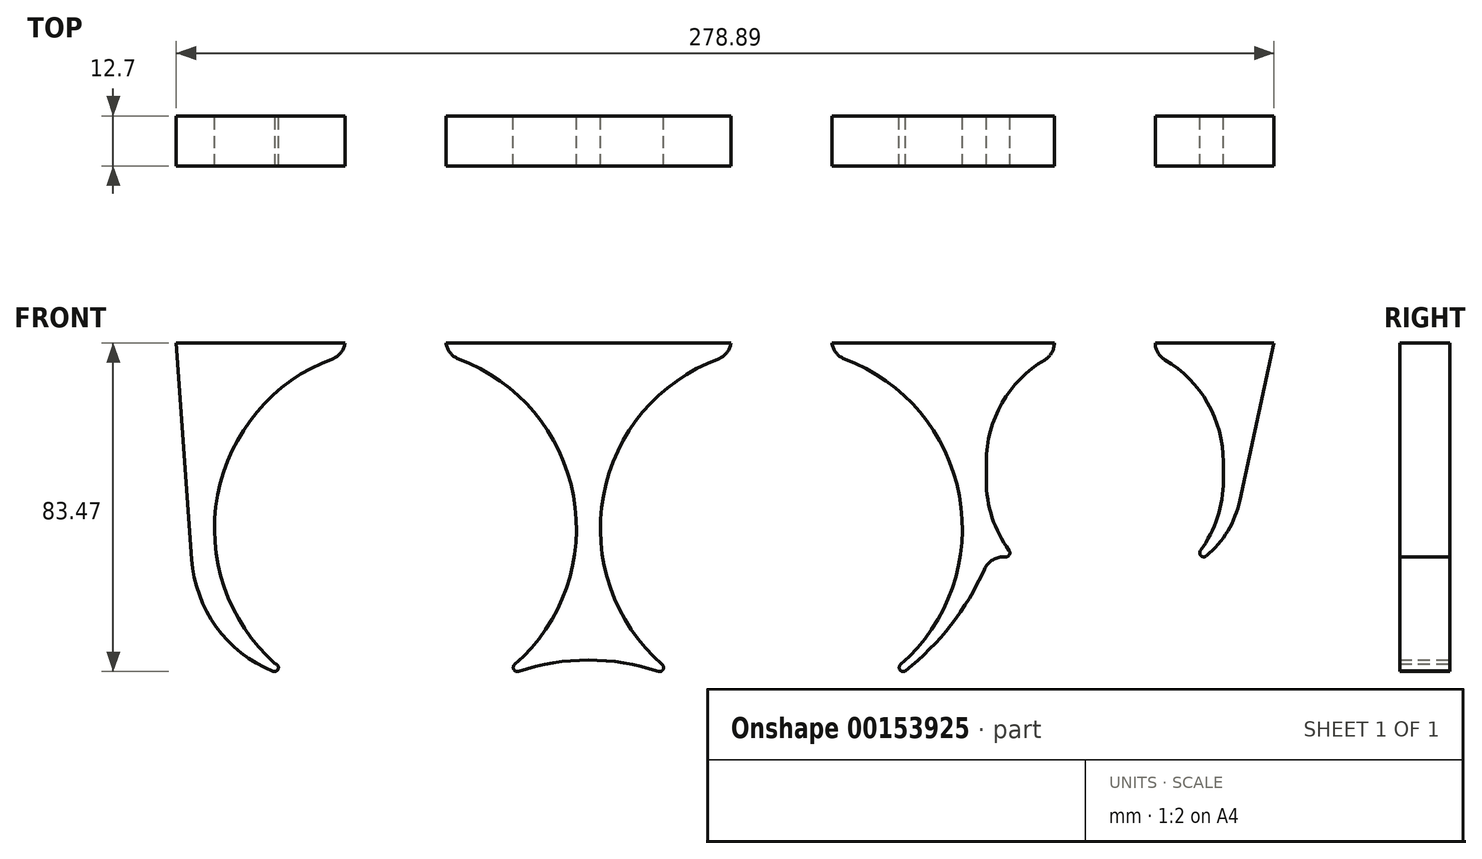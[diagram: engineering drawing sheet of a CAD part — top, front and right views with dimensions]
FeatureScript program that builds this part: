
annotation { "Feature Type Name" : "Feature", "Feature Type Description" : "" }
export const myFeature = defineFeature(function(context is Context, id is Id, definition is map)
    precondition{}
    {
        {
            var Q0;
            Q0=qCreatedBy(makeId("Front.planeOp"),FACE);
            var sketch = newSketch(context, id + "F0", { "sketchPlane" : qUnion([Q0])});
            skArc(sketch, "E0", {"start": v(-61.72, 44.05) * mm, "mid": v(-49.02, -45.85) * mm, "end": v(-36.32, 44.05) * mm, "construction": true});
            skArc(sketch, "E1", {"start": v(36.32, 44.05) * mm, "mid": v(49.02, -45.85) * mm, "end": v(61.72, 44.05) * mm, "construction": true});
            skLineSegment(sketch, "E2", {"start": v(-61.72, 44.05) * mm, "end": v(-61.72, 47.1) * mm, "construction": true});
            skLineSegment(sketch, "E3", {"start": v(-61.72, 47.1) * mm, "end": v(-36.32, 47.1) * mm, "construction": true});
            skLineSegment(sketch, "E4", {"start": v(-36.32, 47.1) * mm, "end": v(-36.32, 44.05) * mm, "construction": true});
            skLineSegment(sketch, "E5", {"start": v(36.32, 44.05) * mm, "end": v(36.32, 47.1) * mm, "construction": true});
            skLineSegment(sketch, "E6", {"start": v(36.32, 47.1) * mm, "end": v(61.72, 47.1) * mm, "construction": true});
            skLineSegment(sketch, "E7", {"start": v(61.72, 47.1) * mm, "end": v(61.72, 44.05) * mm, "construction": true});
            skArc(sketch, "E8", {"start": v(-65, 42.98) * mm, "mid": v(-62.78, 44.58) * mm, "end": v(-61.72, 47.1) * mm, "construction": true});
            skPoint(sketch, "E8.centerSnap0", {"position": v(-49.02, 47.1) * mm});
            skArc(sketch, "E9", {"start": v(-36.32, 47.1) * mm, "mid": v(-35.26, 44.58) * mm, "end": v(-33.05, 42.98) * mm, "construction": true});
            skArc(sketch, "E10", {"start": v(33.05, 42.98) * mm, "mid": v(35.26, 44.58) * mm, "end": v(36.32, 47.1) * mm, "construction": true});
            skArc(sketch, "E11", {"start": v(61.72, 47.1) * mm, "mid": v(62.78, 44.58) * mm, "end": v(65, 42.98) * mm, "construction": true});
            skArc(sketch, "E12", {"start": v(118.5, 44.05) * mm, "mid": v(105.9, 33) * mm, "end": v(101.22, 16.9) * mm, "construction": true});
            skLineSegment(sketch, "E13", {"start": v(118.5, 44.05) * mm, "end": v(118.5, 47.1) * mm, "construction": true});
            skLineSegment(sketch, "E14", {"start": v(118.5, 47.1) * mm, "end": v(143.9, 47.1) * mm, "construction": true});
            skLineSegment(sketch, "E15", {"start": v(143.9, 47.1) * mm, "end": v(143.9, 44.05) * mm, "construction": true});
            skArc(sketch, "E16", {"start": v(115.99, 42.73) * mm, "mid": v(117.82, 44.59) * mm, "end": v(118.5, 47.1) * mm, "construction": true});
            skArc(sketch, "E17", {"start": v(143.9, 47.1) * mm, "mid": v(144.56, 44.59) * mm, "end": v(146.4, 42.73) * mm, "construction": true});
            skArc(sketch, "E18", {"start": v(101.22, 12.13) * mm, "mid": v(131.2, -17.84) * mm, "end": v(161.16, 12.13) * mm, "construction": true});
            skArc(sketch, "E19.trimOffspring", {"start": v(161.16, 16.9) * mm, "mid": v(156.48, 33) * mm, "end": v(143.9, 44.05) * mm, "construction": true});
            skLineSegment(sketch, "E20", {"start": v(101.22, 16.9) * mm, "end": v(101.22, 12.13) * mm, "construction": true});
            skLineSegment(sketch, "E21", {"start": v(161.16, 12.13) * mm, "end": v(161.16, 16.9) * mm, "construction": true});
            skSolve(sketch);
        }
        {
            var Q0;
            Q0=qCreatedBy(makeId("Front.planeOp"),FACE);
            var sketch = newSketch(context, id + "F1", { "sketchPlane" : qUnion([Q0])});
            skLineSegment(sketch, "E22", {"start": v(-36.2, 47.1) * mm, "end": v(36.2, 47.1) * mm});
            skArc(sketch, "E23", {"start": v(-36.2, 47.1) * mm, "mid": v(-35.16, 44.65) * mm, "end": v(-33, 43.1) * mm});
            skArc(sketch, "E24", {"start": v(33, 43.1) * mm, "mid": v(35.16, 44.65) * mm, "end": v(36.2, 47.1) * mm});
            skArc(sketch, "E25", {"start": v(-18.74, -34.6) * mm, "mid": v(-3.8, 8.3) * mm, "end": v(-33, 43.1) * mm});
            skArc(sketch, "E26", {"start": v(33, 43.1) * mm, "mid": v(3.8, 8.3) * mm, "end": v(18.74, -34.6) * mm});
            skArc(sketch, "E27", {"start": v(17.75, -36.32) * mm, "mid": v(0, -33.44) * mm, "end": v(-17.75, -36.32) * mm});
            skPoint(sketch, "E28.visualSharp", {"position": v(-26.96, -40.34) * mm});
            skArc(sketch, "E28.filletArc", {"start": v(-18.74, -34.6) * mm, "mid": v(-18.95, -35.86) * mm, "end": v(-17.75, -36.32) * mm});
            skPoint(sketch, "E29.visualSharp", {"position": v(26.96, -40.34) * mm});
            skArc(sketch, "E29.filletArc", {"start": v(17.75, -36.32) * mm, "mid": v(18.95, -35.86) * mm, "end": v(18.74, -34.6) * mm});
            skSolve(sketch);
        }
        {
            var Q0;
            Q0=makeQuery(id+"F1.imprint","IMPRINT",FACE,{"disambiguationData":[TD([[makeQuery(id+"F1.imprint","IMPRINT",EDGE,{"derivedFrom":sQuery(id+"F1.wireOp",EDGE,"E22")}),-1.0]])]});
            extrude(context, id + "F2", {"entities" : qUnion([Q0]), "depth" : 12.7 * mm});
        }
        {
            var Q0;
            Q0=qCreatedBy(makeId("Front.planeOp"),FACE);
            var sketch = newSketch(context, id + "F3", { "sketchPlane" : qUnion([Q0])});
            skArc(sketch, "E30", {"start": v(-65.04, 43.1) * mm, "mid": v(-94.3, 8) * mm, "end": v(-78.83, -35) * mm});
            skArc(sketch, "E31", {"start": v(-65.04, 43.1) * mm, "mid": v(-62.89, 44.65) * mm, "end": v(-61.85, 47.1) * mm});
            skLineSegment(sketch, "E32", {"start": v(-61.85, 47.1) * mm, "end": v(-104.71, 47.1) * mm});
            skArc(sketch, "E33", {"start": v(-80.16, -36.3) * mm, "mid": v(-78.8, -35.66) * mm, "end": v(-79.56, -34.37) * mm});
            skLineSegment(sketch, "E34", {"start": v(-104.71, 47.1) * mm, "end": v(-100.79, -7.82) * mm});
            skLineSegment(sketch, "E35", {"start": v(-95, 0) * mm, "end": v(-101.35, 0) * mm, "construction": true});
            skArc(sketch, "E36", {"start": v(-100.79, -7.82) * mm, "mid": v(-94.53, -25) * mm, "end": v(-80.16, -36.3) * mm});
            skSolve(sketch);
        }
        {
            var Q0;
            Q0 = qSketchRegion(id + "F3", true);
            extrude(context, id + "F4", {"entities" : qUnion([Q0]), "depth" : 12.7 * mm});
        }
        {
            var Q0;
            Q0=qCreatedBy(makeId("Front.planeOp"),FACE);
            var sketch = newSketch(context, id + "F5", { "sketchPlane" : qUnion([Q0])});
            skArc(sketch, "E37", {"start": v(79.3, -34.6) * mm, "mid": v(94.24, 8.3) * mm, "end": v(65.04, 43.1) * mm});
            skArc(sketch, "E38", {"start": v(115.92, 42.84) * mm, "mid": v(105.06, 31.84) * mm, "end": v(101.1, 16.9) * mm});
            skArc(sketch, "E39", {"start": v(61.85, 47.1) * mm, "mid": v(62.89, 44.65) * mm, "end": v(65.04, 43.1) * mm});
            skArc(sketch, "E40", {"start": v(115.92, 42.84) * mm, "mid": v(117.7, 44.65) * mm, "end": v(118.36, 47.1) * mm});
            skLineSegment(sketch, "E41", {"start": v(61.85, 47.1) * mm, "end": v(118.36, 47.1) * mm});
            skArc(sketch, "E42", {"start": v(79.3, -34.6) * mm, "mid": v(79.18, -36) * mm, "end": v(80.57, -36.18) * mm});
            skArc(sketch, "E43.trimOffspring", {"start": v(80.57, -36.18) * mm, "mid": v(92.12, -24.51) * mm, "end": v(100.56, -10.44) * mm});
            skPoint(sketch, "E44.center.orphan", {"position": v(39.91, 19.05) * mm});
            skArc(sketch, "E45", {"start": v(101.1, 12.13) * mm, "mid": v(102.57, 2.8) * mm, "end": v(106.88, -5.61) * mm});
            skLineSegment(sketch, "E46", {"start": v(101.1, 16.9) * mm, "end": v(101.1, 12.13) * mm});
            skArc(sketch, "E47", {"start": v(105.98, -7.22) * mm, "mid": v(106.94, -6.7) * mm, "end": v(106.88, -5.61) * mm});
            skArc(sketch, "E48", {"start": v(105.98, -7.22) * mm, "mid": v(102.76, -7.97) * mm, "end": v(100.56, -10.44) * mm});
            skSolve(sketch);
        }
        {
            var Q0;
            Q0 = qSketchRegion(id + "F5", true);
            extrude(context, id + "F6", {"entities" : qUnion([Q0]), "depth" : 12.7 * mm});
        }
        {
            var Q0;
            Q0=qCreatedBy(makeId("Front.planeOp"),FACE);
            var sketch = newSketch(context, id + "F7", { "sketchPlane" : qUnion([Q0])});
            skArc(sketch, "E49", {"start": v(161.3, 16.9) * mm, "mid": v(157.32, 31.84) * mm, "end": v(146.46, 42.84) * mm});
            skArc(sketch, "E50", {"start": v(144.02, 47.1) * mm, "mid": v(144.67, 44.65) * mm, "end": v(146.46, 42.84) * mm});
            skLineSegment(sketch, "E51", {"start": v(144.02, 47.1) * mm, "end": v(174.18, 47.1) * mm});
            skArc(sketch, "E52", {"start": v(156.98, -6.99) * mm, "mid": v(162.43, -0.64) * mm, "end": v(165.52, 7.13) * mm});
            skLineSegment(sketch, "E53", {"start": v(174.18, 47.1) * mm, "end": v(165.52, 7.13) * mm});
            skLineSegment(sketch, "E54", {"start": v(161.3, 16.9) * mm, "end": v(167.64, 16.9) * mm, "construction": true});
            skArc(sketch, "E55", {"start": v(155.5, -5.61) * mm, "mid": v(159.8, 2.8) * mm, "end": v(161.3, 12.13) * mm});
            skLineSegment(sketch, "E56", {"start": v(161.3, 12.13) * mm, "end": v(161.3, 16.9) * mm});
            skArc(sketch, "E57", {"start": v(155.5, -5.61) * mm, "mid": v(155.63, -6.95) * mm, "end": v(156.98, -6.99) * mm});
            skSolve(sketch);
        }
        {
            var Q0;
            Q0=makeQuery(id+"F7.imprint","IMPRINT",FACE,{"disambiguationData":[TD([[makeQuery(id+"F7.imprint","IMPRINT",EDGE,{"derivedFrom":sQuery(id+"F7.wireOp",EDGE,"E49")}),-1.0]])]});
            extrude(context, id + "F8", {"entities" : qUnion([Q0]), "depth" : 12.7 * mm});
        }
    });
